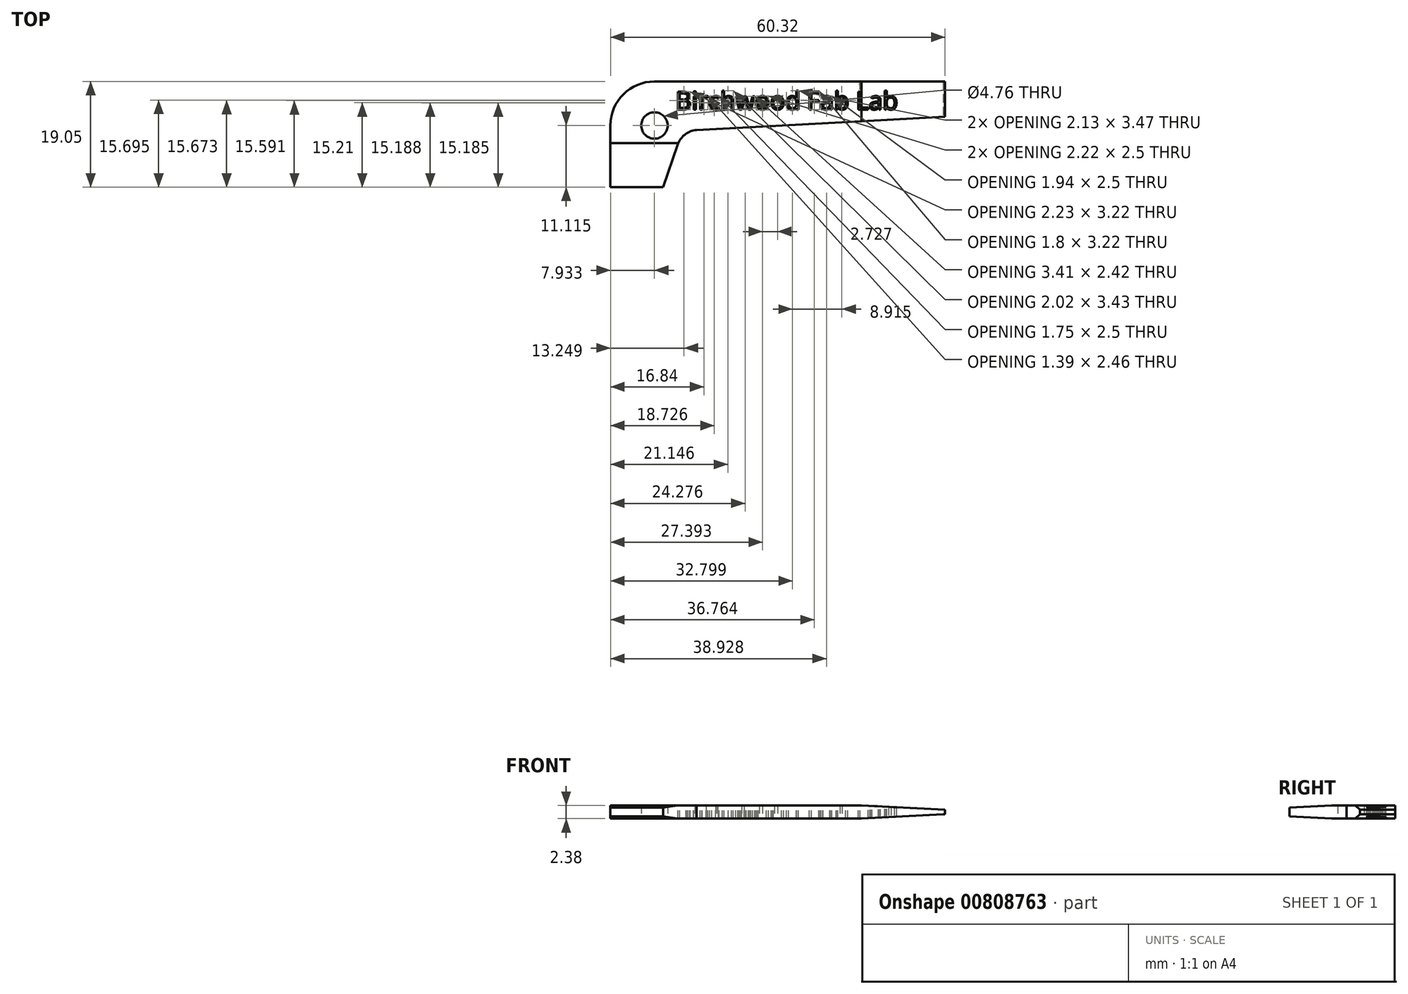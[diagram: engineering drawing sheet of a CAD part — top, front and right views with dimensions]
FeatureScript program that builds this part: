
annotation { "Feature Type Name" : "Feature", "Feature Type Description" : "" }
export const myFeature = defineFeature(function(context is Context, id is Id, definition is map)
    precondition{}
    {
        {
            var Q0;
            Q0=qCreatedBy(makeId("Top.planeOp"),FACE);
            var sketch = newSketch(context, id + "F0", { "sketchPlane" : qUnion([Q0])});
            skLineSegment(sketch, "E0", {"start": v(-53.44, 46.44) * mm, "end": v(6.88, 46.44) * mm});
            skLineSegment(sketch, "E1", {"start": v(-53.44, 46.44) * mm, "end": v(-53.44, 27.4) * mm});
            skLineSegment(sketch, "E2", {"start": v(-53.44, 27.4) * mm, "end": v(-43.92, 27.4) * mm});
            skLineSegment(sketch, "E3", {"start": v(6.88, 46.44) * mm, "end": v(6.88, 40.1) * mm});
            skArc(sketch, "E4", {"start": v(-37.92, 37.7) * mm, "mid": v(-40.02, 36.86) * mm, "end": v(-41.33, 35.02) * mm});
            skLineSegment(sketch, "E5", {"start": v(-43.92, 27.4) * mm, "end": v(-41.33, 35.02) * mm});
            skCircle(sketch, "E6", {"center": v(-45.5, 38.5) * mm, "radius": 2.38 * mm});
            skLineSegment(sketch, "E7", {"start": v(6.88, 40.1) * mm, "end": v(-37.92, 37.7) * mm});
            skSolve(sketch);
        }
        {
            var Q0;
            Q0=makeQuery(id+"F0.imprint","IMPRINT",FACE,{"disambiguationData":[TD([[makeQuery(id+"F0.imprint","IMPRINT",EDGE,{"derivedFrom":sQuery(id+"F0.wireOp",EDGE,"E0")}),-1.0]])]});
            extrude(context, id + "F1", {"entities" : qUnion([Q0]), "depth" : 2.38 * mm, "offsetDistance" : 25.4 * mm});
        }
        {
            var Q0;
            Q0=makeQuery(id+"F1.opExtrude","SWEPT_EDGE",EDGE,{"disambiguationData":[OSD([sQuery(id+"F0.wireOp",EDGE,"E0"),sQuery(id+"F0.wireOp",EDGE,"E1")])]});
            fillet(context, id + "F2", {"entities" : qUnion([Q0]), "radius" : 7.94 * mm, "tangentPropagation" : true, "allowEdgeOverflow" : false});
        }
        {
            var Q0;
            Q0=makeQuery(id+"F1.opExtrude","SWEPT_FACE",FACE,{"disambiguationData":[OSD([sQuery(id+"F0.wireOp",EDGE,"E0")])]});
            var sketch = newSketch(context, id + "F3", { "sketchPlane" : qUnion([Q0])});
            skLineSegment(sketch, "E8", {"start": v(-6.88, 1.6) * mm, "end": v(8.22, 2.38) * mm});
            skLineSegment(sketch, "E9", {"start": v(8.22, 2.38) * mm, "end": v(8.2, 2.73) * mm});
            skLineSegment(sketch, "E10", {"start": v(8.2, 2.73) * mm, "end": v(-7.22, 3.2) * mm});
            skLineSegment(sketch, "E11", {"start": v(-7.22, 3.2) * mm, "end": v(-7.27, 1.55) * mm});
            skLineSegment(sketch, "E12", {"start": v(-7.27, 1.55) * mm, "end": v(-6.88, 1.6) * mm});
            skSolve(sketch);
        }
        {
            var Q0;
            Q0=qSketchRegion(id+"F3",true);
            extrude(context, id + "F4", {"entities" : qUnion([Q0]), "operationType" : NewBodyOperationType.REMOVE, "endBound" : BoundingType.THROUGH_ALL, "oppositeDirection" : true, "depth" : 25.4 * mm, "offsetDistance" : 25.4 * mm});
        }
        {
            var Q0;
            Q0=makeQuery(id+"F1.opExtrude","SWEPT_FACE",FACE,{"disambiguationData":[OSD([sQuery(id+"F0.wireOp",EDGE,"E7")])]});
            var sketch = newSketch(context, id + "F5", { "sketchPlane" : qUnion([Q0])});
            skLineSegment(sketch, "E13", {"start": v(-6.08, 0) * mm, "end": v(9.01, 0.8) * mm});
            skLineSegment(sketch, "E14", {"start": v(9.01, 0.8) * mm, "end": v(9.01, 0) * mm});
            skLineSegment(sketch, "E15", {"start": v(9.01, 0) * mm, "end": v(-6.08, 0) * mm});
            skLineSegment(sketch, "E16", {"start": v(-6.08, 0) * mm, "end": v(-6.08, 0) * mm});
            skSolve(sketch);
        }
        {
            var Q0;
            Q0=qSketchRegion(id+"F5",true);
            extrude(context, id + "F6", {"entities" : qUnion([Q0]), "operationType" : NewBodyOperationType.REMOVE, "endBound" : BoundingType.THROUGH_ALL, "oppositeDirection" : true, "depth" : 25.4 * mm, "offsetDistance" : 25.4 * mm});
        }
        {
            var Q0;
            Q0=makeQuery(id+"F1.opExtrude","SWEPT_FACE",FACE,{"disambiguationData":[OSD([sQuery(id+"F0.wireOp",EDGE,"E0")])]});
            var sketch = newSketch(context, id + "F7", { "sketchPlane" : qUnion([Q0])});
            skLineSegment(sketch, "E17", {"start": v(-6.88, 0.8) * mm, "end": v(-6.54, 0.8) * mm});
            skLineSegment(sketch, "E18", {"start": v(-6.54, 0.8) * mm, "end": v(-6.54, -0.1) * mm});
            skLineSegment(sketch, "E19", {"start": v(-6.54, -0.1) * mm, "end": v(-6.98, -0.1) * mm});
            skLineSegment(sketch, "E20", {"start": v(-6.98, -0.1) * mm, "end": v(-6.98, 0.8) * mm});
            skLineSegment(sketch, "E21", {"start": v(-6.98, 0.8) * mm, "end": v(-6.88, 0.8) * mm});
            skSolve(sketch);
        }
        {
            var Q0;
            Q0=qSketchRegion(id+"F7",true);
            extrude(context, id + "F8", {"entities" : qUnion([Q0]), "operationType" : NewBodyOperationType.REMOVE, "endBound" : BoundingType.THROUGH_ALL, "oppositeDirection" : true, "depth" : 25.4 * mm, "offsetDistance" : 25.4 * mm});
        }
        {
            var Q0;
            Q0=makeQuery(id+"F1.opExtrude","SWEPT_FACE",FACE,{"disambiguationData":[OSD([sQuery(id+"F0.wireOp",EDGE,"E1")])]});
            var sketch = newSketch(context, id + "F9", { "sketchPlane" : qUnion([Q0])});
            skPoint(sketch, "E22", {"position": v(-27.4, 1.98) * mm});
            skPoint(sketch, "E23", {"position": v(-27.4, 0.4) * mm});
            skPoint(sketch, "E24", {"position": v(-35.33, 2.38) * mm});
            skPoint(sketch, "E25", {"position": v(-35.34, 0) * mm});
            skLineSegment(sketch, "E26", {"start": v(-27.4, 1.98) * mm, "end": v(-35.33, 2.38) * mm});
            skLineSegment(sketch, "E27", {"start": v(-35.33, 2.38) * mm, "end": v(-26.71, 2.73) * mm});
            skLineSegment(sketch, "E28", {"start": v(-26.71, 2.73) * mm, "end": v(-26.68, 1.98) * mm});
            skLineSegment(sketch, "E29", {"start": v(-26.68, 1.98) * mm, "end": v(-27.4, 1.98) * mm});
            skLineSegment(sketch, "E30", {"start": v(-27.4, 0.4) * mm, "end": v(-35.34, 0) * mm});
            skLineSegment(sketch, "E31", {"start": v(-35.34, 0) * mm, "end": v(-35.01, -0.3) * mm});
            skLineSegment(sketch, "E32", {"start": v(-35.01, -0.3) * mm, "end": v(-26.82, -0.3) * mm});
            skLineSegment(sketch, "E33", {"start": v(-26.82, -0.3) * mm, "end": v(-26.94, 0.4) * mm});
            skLineSegment(sketch, "E34", {"start": v(-26.94, 0.4) * mm, "end": v(-27.4, 0.4) * mm});
            skSolve(sketch);
        }
        {
            var Q0;
            Q0=qSketchRegion(id+"F9",true);
            extrude(context, id + "F10", {"entities" : qUnion([Q0]), "operationType" : NewBodyOperationType.REMOVE, "endBound" : BoundingType.THROUGH_ALL, "oppositeDirection" : true, "depth" : 25.4 * mm, "offsetDistance" : 25.4 * mm});
        }
        {
            var Q0;
            Q0=makeQuery(id+"F1.opExtrude","CAP_FACE",FACE,{"disambiguationData":[OSD([sQuery(id+"F0.wireOp",EDGE,"E0"),sQuery(id+"F0.wireOp",EDGE,"E1"),sQuery(id+"F0.wireOp",EDGE,"E2"),sQuery(id+"F0.wireOp",EDGE,"E3"),sQuery(id+"F0.wireOp",EDGE,"E4"),sQuery(id+"F0.wireOp",EDGE,"E5"),sQuery(id+"F0.wireOp",EDGE,"E6"),sQuery(id+"F0.wireOp",EDGE,"E7")])],"isStart":false});
            var sketch = newSketch(context, id + "F11", { "sketchPlane" : qUnion([Q0])});
            skText(sketch, "E35", { "text": "Birchwood Fab Lab", "fontName": "OpenSans-Regular.ttf"});
            const initialGuessF11  = {"E35": [-0.04175, 0.04137, 1, 0, 0.00325]};
            skSetInitialGuess(sketch, initialGuessF11);
            skSolve(sketch);
        }
        {
            var Q0;
            Q0 = qSketchRegion(id + "F11", true);
            extrude(context, id + "F12", {"entities" : qUnion([Q0]), "operationType" : NewBodyOperationType.REMOVE, "oppositeDirection" : true, "depth" : 3.8 * mm, "offsetDistance" : 25.4 * mm});
        }
    });
